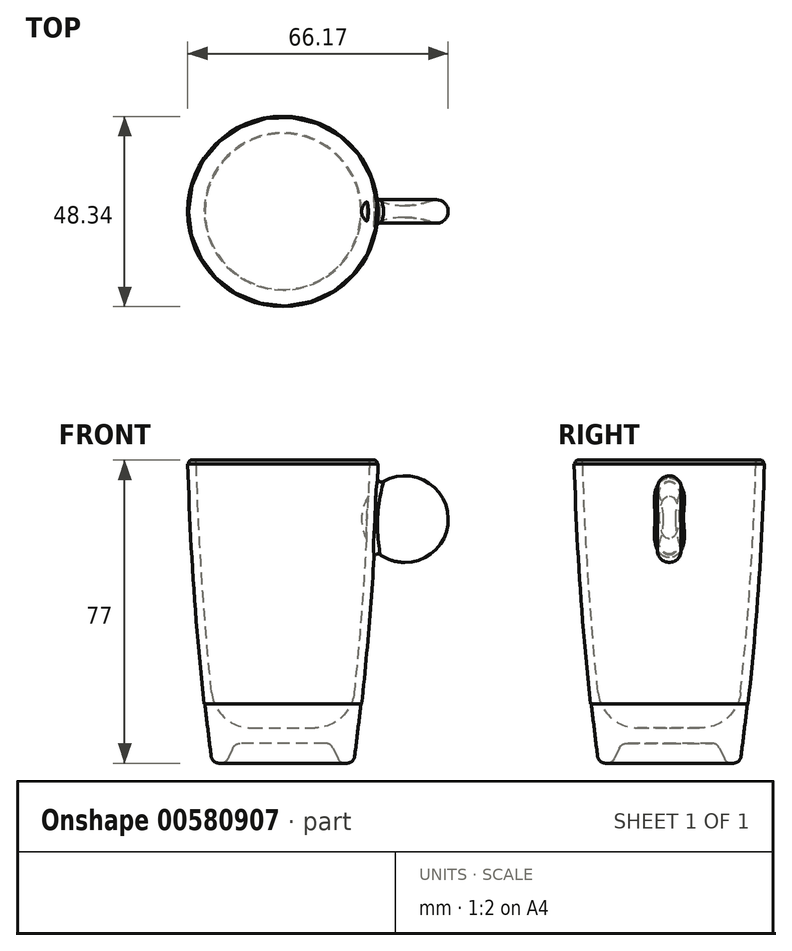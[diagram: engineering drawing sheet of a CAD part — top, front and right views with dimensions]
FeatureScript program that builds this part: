
annotation { "Feature Type Name" : "Feature", "Feature Type Description" : "" }
export const myFeature = defineFeature(function(context is Context, id is Id, definition is map)
    precondition{}
    {
        {
            var Q0;
            Q0=qCreatedBy(makeId("Front.planeOp"),FACE);
            var sketch = newSketch(context, id + "F0", { "sketchPlane" : qUnion([Q0])});
            skLineSegment(sketch, "E0", {"start": v(0, 5) * mm, "end": v(12.17, 5) * mm});
            skLineSegment(sketch, "E1", {"start": v(12.17, 5) * mm, "end": v(14.5, 0) * mm});
            skLineSegment(sketch, "E2", {"start": v(14.5, 0) * mm, "end": v(18, 0) * mm});
            skArc(sketch, "E3", {"start": v(18, 0) * mm, "mid": v(21.98, 38.42) * mm, "end": v(24, 77) * mm});
            skLineSegment(sketch, "E4", {"start": v(24, 77) * mm, "end": v(22, 77) * mm});
            skLineSegment(sketch, "E5", {"start": v(0, 9) * mm, "end": v(0, 5) * mm});
            skLineSegment(sketch, "E6", {"start": v(17.1, 9) * mm, "end": v(0, 9) * mm});
            skArc(sketch, "E7.trimOffspring", {"start": v(17.1, 9) * mm, "mid": v(20.32, 42.94) * mm, "end": v(22, 77) * mm});
            skPoint(sketch, "E8.orphan", {"position": v(0, 77) * mm});
            skSolve(sketch);
        }
        {
            var Q0;
            Q0=qSketchRegion(id+"F0",true);
            var Q1;
            Q1=sQuery(id+"F0.wireOp",EDGE,"E5");
            revolve(context, id + "F1", {"entities" : qUnion([Q0]), "axis" : qUnion([Q1]), "revolveType" : RevolveType.FULL});
        }
        {
            var Q0;
            Q0=makeQuery(id+"F1.opRevolve","SWEPT_EDGE",EDGE,{"disambiguationData":[OSD([sQuery(id+"F0.wireOp",EDGE,"E4"),sQuery(id+"F0.wireOp",EDGE,"E7.trimOffspring")])]});
            var Q1;
            Q1=makeQuery(id+"F1.opRevolve","SWEPT_EDGE",EDGE,{"disambiguationData":[OSD([sQuery(id+"F0.wireOp",EDGE,"E3"),sQuery(id+"F0.wireOp",EDGE,"E4")])]});
            fillet(context, id + "F2", {"entities" : qUnion([Q0, Q1]), "radius" : .8 * mm, "tangentPropagation" : true, "allowEdgeOverflow" : false});
        }
        {
            var Q0;
            Q0=makeQuery(id+"F1.opRevolve","SWEPT_EDGE",EDGE,{"disambiguationData":[OSD([sQuery(id+"F0.wireOp",EDGE,"E2"),sQuery(id+"F0.wireOp",EDGE,"E3")])]});
            var Q1;
            Q1=makeQuery(id+"F1.opRevolve","SWEPT_EDGE",EDGE,{"disambiguationData":[OSD([sQuery(id+"F0.wireOp",EDGE,"E1"),sQuery(id+"F0.wireOp",EDGE,"E2")])]});
            var Q2;
            Q2=makeQuery(id+"F1.opRevolve","SWEPT_EDGE",EDGE,{"disambiguationData":[OSD([sQuery(id+"F0.wireOp",EDGE,"E0"),sQuery(id+"F0.wireOp",EDGE,"E1")])]});
            fillet(context, id + "F3", {"entities" : qUnion([Q0, Q1, Q2]), "radius" : 2 * mm, "tangentPropagation" : true, "allowEdgeOverflow" : false});
        }
        {
            var Q0;
            Q0=makeQuery(id+"F1.opRevolve","SWEPT_EDGE",EDGE,{"disambiguationData":[OSD([sQuery(id+"F0.wireOp",EDGE,"E6"),sQuery(id+"F0.wireOp",EDGE,"E7.trimOffspring")])]});
            fillet(context, id + "F4", {"entities" : qUnion([Q0]), "radius" : 10 * mm, "tangentPropagation" : true, "allowEdgeOverflow" : false});
        }
        {
            var Q0;
            Q0=qCreatedBy(makeId("Front.planeOp"),FACE);
            var sketch = newSketch(context, id + "F5", { "sketchPlane" : qUnion([Q0])});
            skArc(sketch, "E9", {"start": v(19.8, 15) * mm, "mid": v(22.5, 45.46) * mm, "end": v(23.97, 76) * mm});
            skLineSegment(sketch, "E10", {"start": v(19.8, 15) * mm, "end": v(20, 15) * mm});
            skLineSegment(sketch, "E11", {"start": v(23.97, 76) * mm, "end": v(24.17, 76) * mm});
            skArc(sketch, "E12", {"start": v(20, 15) * mm, "mid": v(22.7, 45.46) * mm, "end": v(24.17, 76) * mm});
            skSolve(sketch);
        }
        {
            var Q0;
            Q0=qSketchRegion(id+"F5",true);
            var Q1;
            Q1=sQuery(id+"F0.wireOp",EDGE,"E5");
            revolve(context, id + "F6", {"operationType" : NewBodyOperationType.ADD, "entities" : qUnion([Q0]), "axis" : qUnion([Q1]), "revolveType" : RevolveType.FULL});
        }
        {
            var Q0;
            Q0=makeQuery(id+"F1.opRevolve","SWEPT_FACE",FACE,{"disambiguationData":[OSD([sQuery(id+"F0.wireOp",EDGE,"E4")])]});
            cPlane(context, id + "F7", {"entities" : qUnion([Q0]), "cplaneType" : CPlaneType.OFFSET, "offset" : 15 * mm, "oppositeDirection" : true, "width" : 150 * mm, "height" : 150 * mm});
        }
        {
            var Q0;
            Q0=qCreatedBy(id+"F7.planeOp",FACE);
            var sketch = newSketch(context, id + "F8", { "sketchPlane" : qUnion([Q0])});
            skArc(sketch, "E13", {"start": v(42, 0) * mm, "mid": v(40.7, 2.48) * mm, "end": v(37.91, 2.8) * mm});
            skArc(sketch, "E14", {"start": v(31, 1.5) * mm, "mid": v(34.52, 1.83) * mm, "end": v(37.91, 2.8) * mm});
            skLineSegment(sketch, "E15", {"start": v(31, 1.5) * mm, "end": v(31, 0) * mm});
            skLineSegment(sketch, "E16.MirrorCS", {"start": v(31, -1.5) * mm, "end": v(31, 0) * mm});
            skArc(sketch, "E17.MirrorCS", {"start": v(31, -1.5) * mm, "mid": v(34.52, -1.83) * mm, "end": v(37.91, -2.8) * mm});
            skArc(sketch, "E18.MirrorCS", {"start": v(42, 0) * mm, "mid": v(40.7, -2.48) * mm, "end": v(37.91, -2.8) * mm});
            skSolve(sketch);
        }
        {
            var Q0;
            Q0=makeQuery(id+"F8.imprint","IMPRINT",FACE,{"disambiguationData":[TD([[makeQuery(id+"F8.imprint","IMPRINT",EDGE,{"derivedFrom":sQuery(id+"F8.wireOp",EDGE,"E13")}),1.0]])]});
            var Q1;
            Q1=sQuery(id+"F8.wireOp",EDGE,"E16.MirrorCS");
            revolve(context, id + "F9", {"operationType" : NewBodyOperationType.ADD, "entities" : qUnion([Q0]), "axis" : qUnion([Q1]), "revolveType" : RevolveType.FULL});
        }
        {
            var Q0;
            Q0=makeQuery(id+"F9.boolean.opBoolean","INTERSECT",EDGE,{"derivedFrom":[makeQuery(id+"F6.opRevolve","SWEPT_FACE",FACE,{"disambiguationData":[OSD([sQuery(id+"F5.wireOp",EDGE,"E12")])]}),makeQuery(id+"F9.opRevolve","SWEPT_FACE",FACE,{"disambiguationData":[OSD([sQuery(id+"F8.wireOp",EDGE,"E13"),sQuery(id+"F8.wireOp",EDGE,"E18.MirrorCS")])]})]});
            fillet(context, id + "F10", {"entities" : qUnion([Q0]), "radius" : 1 * mm, "tangentPropagation" : true, "allowEdgeOverflow" : false});
        }
    });
